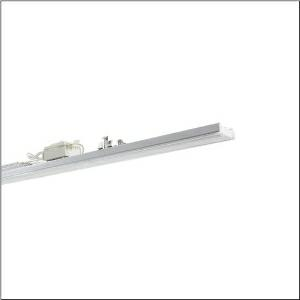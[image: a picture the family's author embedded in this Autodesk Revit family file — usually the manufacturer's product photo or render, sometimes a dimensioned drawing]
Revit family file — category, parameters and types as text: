
# Revit family: licross_r__11_recessed_mo_51te197n485g_8a1d
name_source: partatom
category: Lighting Fixtures
units: mm (PartAtom-declared; Revit-internal decimal feet)

## family parameters
Cut with Voids When Loaded = No
Host = Face
Light Source = No
Part Type = Normal
Room Calculation Point = No
Round Connector Dimension = Use Diameter
Shared = No

## types (1)
- Licross® 11 Recessed MO (1 x LED, 8580 lm, 48.5 W, 4000K)
    Apparent Load = 49 VA
    CIE Flux Codes = 55 90 98 100 100
    Color Rendering = 80
    Color Temperature = 4000K
    Default Elevation = 1800 mm
    Description = Licross® 11 Recessed MO, luminaire insert, of sheet steel, galvanised, coil coated, white, length: 1.500mm, width: 66mm, height: 67mm, LED rated luminous flux: 8.580lm, light colour: 840, control gear: ON/OFF, with plug, 3-pole, with phase selection, mains connection: 220..240V, AC, 50/60Hz, rated input power: 49W, halogen-free wiring, primary light control with lens, of plastic, primary optical cover: cover, of PMMA, light emission: direct distribution, primary light characteristic: double asymmetric, protection rating (complete): IP54, insulation class (complete): insulation class I (protective earthing), certification: CE, ENEC, VDE, UKCA, protection symbol: D if used in an environment with non-conductive dust loads with corresponding accessories, impact resistance: IK06, permissible ambient temperature for indoor applications: -35..+35°C, corresponds to IFS (International Featured Standards) requirements for safety and quality in the food industry, reducing of maximum allowable ambient temperature of 5°C with ceiling mounting, packaging unit: 1 piece
    Height = 58 mm
    Lamp = 1 x LED
    Lamp Light Flux = 8580 lm
    Lamp Power = 48.5 W
    Lamp count = 1
    Length = 1500 mm
    Luminous efficacy = 177 lm/W
    Manufacturer = Siteco
    ModVariant = No
    Model = 51TE197N485G
    Mounting Place = Ceiling
    Mounting Type = Pendant
    Number of Poles = 1
    OnlyDefault = Yes
    Power Factor = 1
    Product Name = Licross® 11 Recessed MO
    Product group = luminaire insert
    ProductGroupID = 902
    Protection Class = Protection class I
    Protection Degree = IP 54
    RLX_Detail_Level = 1
    RLX_Emergency_Light_Flux = 0 lm
    RLX_Emergency_Type = 0
    RLX_Emergency_Type_DB = No
    RlxData = <blob elided: 20793 chars, md5=6f35aadc>
    Socket = socket
    Standby Power = 0 W
    System Light Flux = 8580 lm
    System Power = 49 W
    Type Comments = Product without accessories
    Type Image = l_1296930.jpg
    URL = http://relux.com
    VarID = ---
    Voltage = 0 V
    Weight = 0.00 kg
    Width = 66 mm

## geometry (parser evidence)
native form markers: Blend x4, Sweep x10
no freeform markers — native parametric forms only
